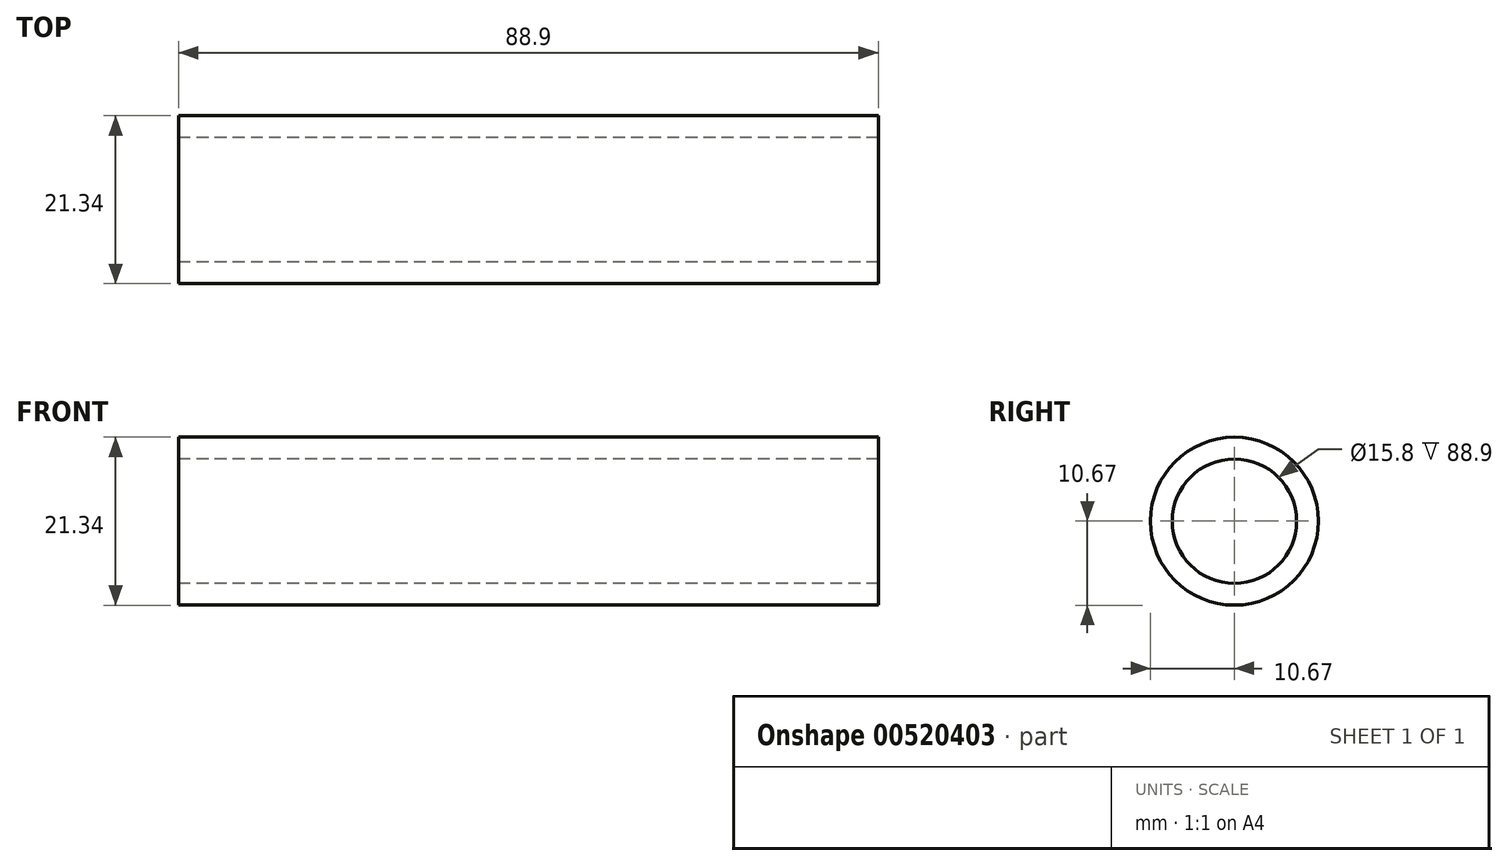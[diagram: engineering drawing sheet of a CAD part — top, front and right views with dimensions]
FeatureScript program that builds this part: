
annotation { "Feature Type Name" : "Feature", "Feature Type Description" : "" }
export const myFeature = defineFeature(function(context is Context, id is Id, definition is map)
    precondition{}
    {
        {
            var Q0;
            Q0=qCreatedBy(makeId("Right.planeOp"),FACE);
            var sketch = newSketch(context, id + "F0", { "sketchPlane" : qUnion([Q0])});
            skCircle(sketch, "E0", {"center": v(0, 0) * mm, "radius": 7.9 * mm});
            skCircle(sketch, "E1", {"center": v(0, 0) * mm, "radius": 10.67 * mm});
            skSolve(sketch);
        }
        {
            var Q0;
            Q0=makeQuery(id+"F0.imprint","IMPRINT",FACE,{"disambiguationData":[TD([[makeQuery(id+"F0.imprint","IMPRINT",EDGE,{"derivedFrom":sQuery(id+"F0.wireOp",EDGE,"E0")}),-1.0]])]});
            extrude(context, id + "F1", {"entities" : qUnion([Q0]), "depth" : 63.5 * mm, "offsetDistance" : 25.4 * mm});
        }
        {
            var Q0;
            Q0=makeQuery(id+"F1.opExtrude","CAP_FACE",FACE,{"disambiguationData":[OSD([sQuery(id+"F0.wireOp",EDGE,"E0"),sQuery(id+"F0.wireOp",EDGE,"E1")])],"isStart":true});
            extrude(context, id + "F2", {"entities" : qUnion([Q0]), "operationType" : NewBodyOperationType.ADD, "depth" : 25.4 * mm, "offsetDistance" : 25.4 * mm});
        }
    });
